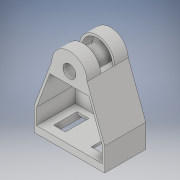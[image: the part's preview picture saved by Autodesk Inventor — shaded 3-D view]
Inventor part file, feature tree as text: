
AUTODESK INVENTOR PART (.ipt)
format: ipt  version: 2019 (Build 230136000, 136)  size: 447,488 bytes
history: native  units: mm
features: sketch x9, extrude x7, plane x2, shell x1, thicken_offset x1, hole x1, projected_geometry x1
ambient origin geometry x8: Origin, YZ Plane, XZ Plane, XY Plane, X Axis, Y Axis, Z Axis, Center Point
bodies: Solid1 (feature_tree)
feature tree (22):
  extrude  "Extrusion1"  Depth=5.5mm
  shell  "Shell2"  Thickness=17.5mm
  thicken_offset  "Thicken5"
  extrude  "Extrusion6"  Depth=30.0mm
  extrude  "Extrusion7"  Depth=2.0mm
  sketch  "Sketch14"  dims[d70=2.0mm d74=21.0mm]
  plane  "Work Plane2"
  hole  "Hole3"  [1 undecoded]
  extrude  "Extrusion9"  Depth=4.5mm
  extrude  "Extrusion10"  Depth=1.25mm
  plane  "Work Plane3"
  extrude  "Extrusion11"  Depth=5.0mm
  extrude  "Extrusion13"  Depth=2.5mm
  sketch  "Sketch1"  dims[d0=15.0mm d8=5.5mm d9=17.5mm d10=0.0mm]
  sketch  "Sketch12"  dims[d32=1.0mm d67=30.0mm]
  projected_geometry  "Projected Loop9"
  sketch  "Sketch13"  dims[d68=30.0mm d69=2.0mm]
  sketch  "Sketch16"  dims[d75=15.0mm d77=4.5mm]
  sketch  "Sketch17"  dims[d78=4.5mm d79=1.25mm]
  sketch  "Sketch18"  dims[d80=2.0mm d81=0.0mm d82=5.0mm]
  sketch  "Sketch19"  dims[d83=10.0mm d84=2.5mm]
  sketch  "Sketch22"  dims[d85=2.5mm d86=5.0mm d87=10.0mm d88=2.5mm d89=2.5mm d90=2.0mm d91=0.0mm d96=10.0mm d97=5.0mm d98=3.4mm d99=6.0mm d100=11.0mm d101=2.6mm d102=90.0deg d103=8.0mm d104=20.594885mm d105=9.5mm d106=2.0mm d107=0.0mm d108=5.5mm d109=2.0mm d110=0.0mm d111=15.0mm d112=6.0mm d113=4.0mm d114=0.0mm d117=5.0mm d118=2.0mm d119=0.0mm]
note: 1 required parameter value undecoded (feature->parameter linkage not recoverable at this tier; creation-order binding heuristic only, values carry confidence <= 0.55)
